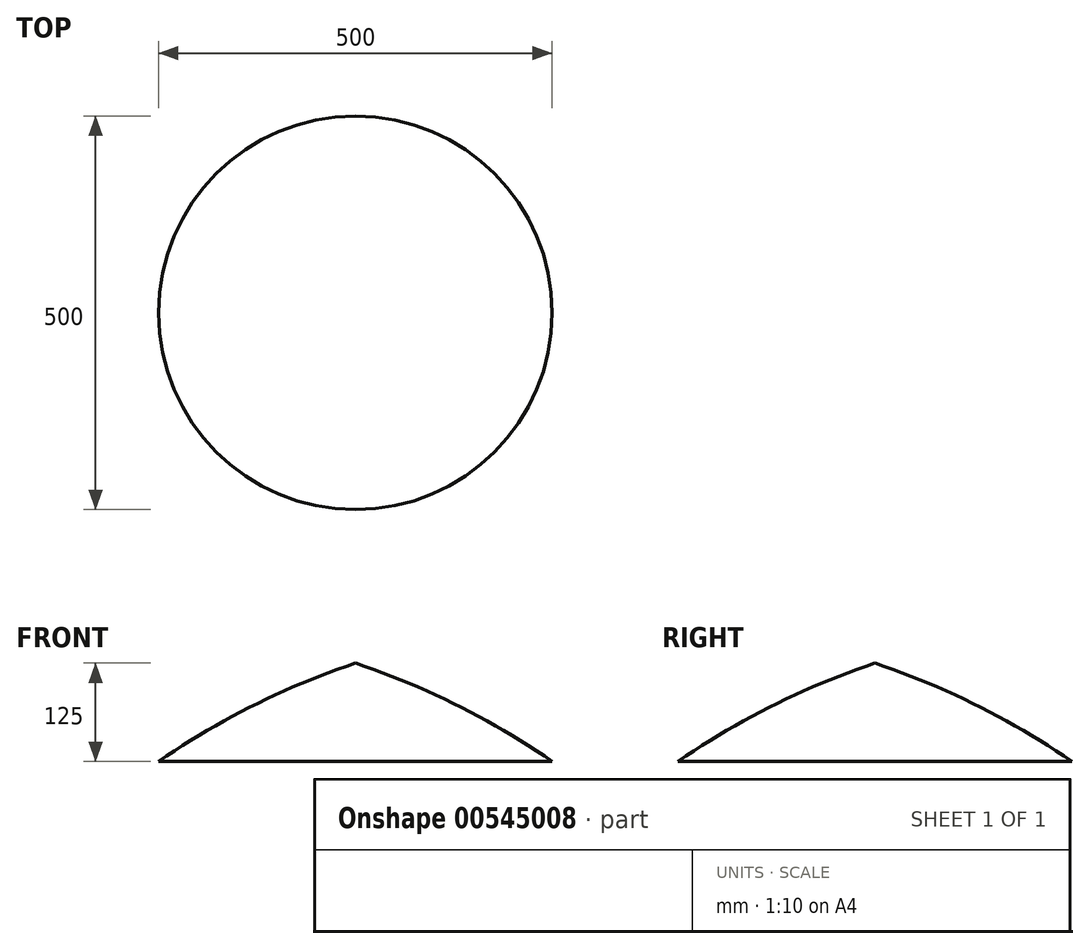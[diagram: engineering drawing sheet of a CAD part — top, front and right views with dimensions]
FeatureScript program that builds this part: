
annotation { "Feature Type Name" : "Feature", "Feature Type Description" : "" }
export const myFeature = defineFeature(function(context is Context, id is Id, definition is map)
    precondition{}
    {
        {
            var Q0;
            Q0=qCreatedBy(makeId("Front.planeOp"),FACE);
            var sketch = newSketch(context, id + "F0", { "sketchPlane" : qUnion([Q0])});
            skLineSegment(sketch, "E0", {"start": v(0, 0) * mm, "end": v(0, 125) * mm});
            skLineSegment(sketch, "E1", {"start": v(0, 0) * mm, "end": v(250, 0) * mm});
            skArc(sketch, "E2", {"start": v(250, 0) * mm, "mid": v(129.39, 71.28) * mm, "end": v(0, 125) * mm});
            skSolve(sketch);
        }
        {
            var Q0;
            Q0=makeQuery(id+"F0.imprint","IMPRINT",FACE,{"disambiguationData":[TD([[makeQuery(id+"F0.imprint","IMPRINT",EDGE,{"derivedFrom":sQuery(id+"F0.wireOp",EDGE,"E0")}),-1.0]])]});
            var Q1;
            Q1=sQuery(id+"F0.wireOp",EDGE,"E2");
            var Q2;
            Q2=sQuery(id+"F0.wireOp",EDGE,"E0");
            revolve(context, id + "F1", {"bodyType" : ToolBodyType.SURFACE, "entities" : qUnion([Q0]), "surfaceEntities" : qUnion([Q1]), "axis" : qUnion([Q2]), "revolveType" : RevolveType.FULL});
        }
    });
